# Revit family: 15.1 Вытяжной крышный вентилятор KW 94-100
name_source: partatom
category: Оборудование
revit_build: Autodesk Revit 2016 (Build: 20151209_0715(x64)
units: mm (PartAtom-declared; Revit-internal decimal feet)

## family parameters
Всегда вертикально = Да
На основе рабочей плоскости = Нет
Общий = Нет
При загрузке вырезать с полостями = Нет
Размер круглого соединителя = Использовать диаметр
Тип детали = Нормальный
Точка расчета площади = Нет

## types (4) — shared parameters
h = 43 мм
Единица измерения = шт.
Завод изготовитель = KORF
Ключевая пометка = Вентиляция
Материал = Сталь серая
Наименование и тех.хар-ка = Вытяжной крышный вентилятор
Напряжение U,В = 3-380
Раздел = ОВ

## per-type parameters (varying)
| type | А | А1 | Б | Б1 | Б2 | Высота | Ж | З | Масса единицы | Мощность, кВт | Сила тока J, А | Тип, марка, обозначение | Частота вращения n, об/мин | Ширина | отступ |
| 94/56-4D | 942 мм | 1150 мм | 570 мм | 399 мм | 810 мм | 942 мм | 236 мм | 565 мм | 155 кг | 3 Вт | 6,7 | KW 94/56-4D | 1400 | 942 мм | 94 мм |
| 94/63-4D | 942 мм | 1150 мм | 570 мм | 399 мм | 860 мм | 942 мм | 236 мм | 565 мм | 205 кг | 6 Вт | 11.7 | KW 94/63-4D | 1430 | 942 мм | 94 мм |
| 94/63-6D | 942 мм | 1150 мм | 570 мм | 399 мм | 860 мм | 942 мм | 236 мм | 565 мм | 185 кг | 2 Вт | 5.6 | KW 94/63-6D | 940 | 942 мм | 94 мм |
| 100/71-6D | 1038 мм | 1345 мм | 655 мм | 459 мм | 905 мм | 1038 мм | 260 мм | 623 мм | 225 кг | 2 Вт | 5.6 | KW 100/71-6D | 940 | 1038 мм | 104 мм |
